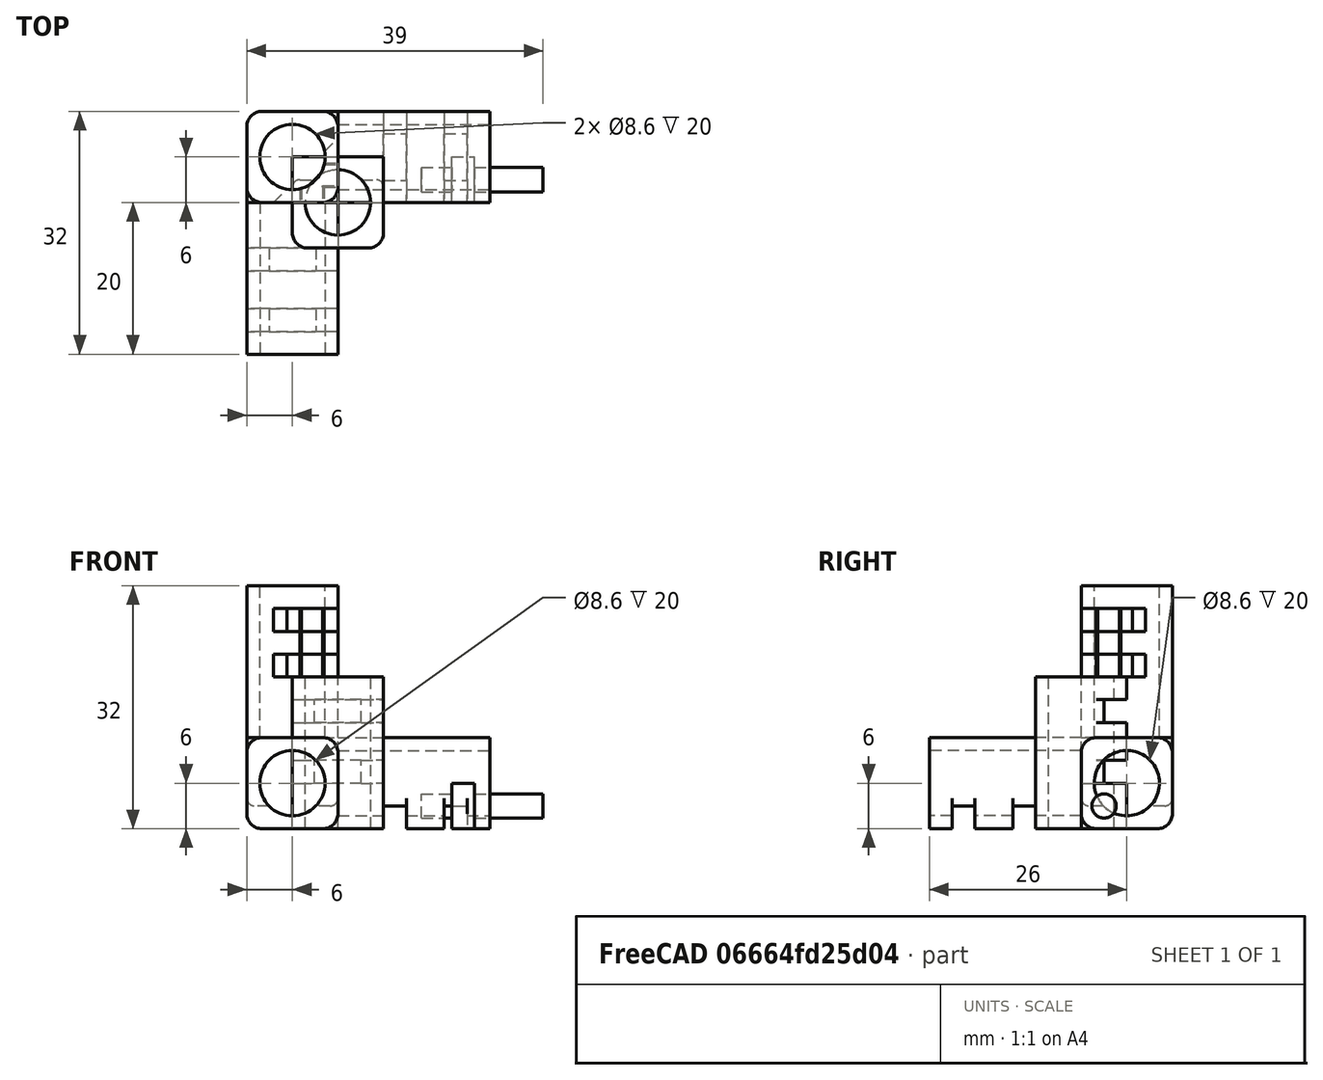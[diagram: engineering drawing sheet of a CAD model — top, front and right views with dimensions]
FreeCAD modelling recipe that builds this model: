
FCSTD DOCUMENT  (FreeCAD 0.18R14555 (Git shallow))
Label: tmp-ecnlose
License: All rights reserved
LicenseURL: http://en.wikipedia.org/wiki/All_rights_reserved
objects: Part::Box×12, Part::Fillet×7, Part::MultiFuse×5, Part::Cut×5, Part::Cylinder×4, Part::Feature×2
note: 35 computed .brp shape members not serialized (recipe doc carries the construction recipe); baked Part::Feature solids carry a one-line shape summary decoded from their .brp

FEATURE [Part::Cylinder] Cylinder
  Angle = 360
  AttacherType = Attacher::AttachEngine3D
  Height = 20
  Radius = 4.3
FEATURE [Part::Box] Box  label="Cube"
  AttacherType = Attacher::AttachEngine3D
  Height = 20
  Length = 12
  Placement = pos=(-6,-6,0) rot=(0,0,1;0rad)
  Width = 12
FEATURE [Part::Box] Box001  label="Cube001"
  AttacherType = Attacher::AttachEngine3D
  Height = 6
  Length = 3
  Placement = pos=(15,0,0) rot=(0,0,1;0rad)
  Width = 6
FEATURE [Part::Cylinder] Cylinder001
  Angle = 360
  AttacherType = Attacher::AttachEngine3D
  Height = 16
  Placement = pos=(11,3,3) rot=(0,1,0;1.5708rad)
  Radius = 1.6
FEATURE [Part::MultiFuse] Fusion
  Shapes = -> [Cylinder001,Box001]
FEATURE [Part::Cut] Cut
  Base = -> Box
  Tool = -> Cylinder
FEATURE [Part::Box] Box002  label="Cube002"
  AttacherType = Attacher::AttachEngine3D
  Height = 3
  Length = 12
  Placement = pos=(-6,3,14) rot=(0,0,1;0rad)
  Width = 3
FEATURE [Part::Box] Box003  label="Cube003"
  AttacherType = Attacher::AttachEngine3D
  Height = 3
  Length = 12
  Placement = pos=(-6,3,6) rot=(0,0,1;0rad)
  Width = 3
FEATURE [Part::MultiFuse] Fusion001
  Shapes = -> [Box003,Box002]
FEATURE [Part::Cut] Cut001
  Base = -> Cut
  Tool = -> Fusion001
FEATURE [Part::Fillet] Fillet
  Base = -> Cut001
  Edges = 2 edges r=2: [Edge12,Edge46]
FEATURE [Part::Fillet] Fillet001
  Base = -> Fillet
  Edges = 4 edges r=1: [Edge7,Edge10,Edge53,Edge54]
FEATURE [Part::Feature] Fillet001001  label="Fillet002"
  Placement = pos=(-6,1.3e-15,6) rot=(0,-0.707107,0.707107;3.14159rad)
  shape: bbox 12 x 20 x 12 mm, 23 faces (baked)
FEATURE [Part::Feature] Fillet001002  label="Fillet003"
  Placement = pos=(1.8e-15,6,6) rot=(0.57735,-0.57735,0.57735;4.18879rad)
  shape: bbox 20 x 12 x 12 mm, 23 faces (baked)
FEATURE [Part::Box] Box004  label="Cube004"
  AttacherType = Attacher::AttachEngine3D
  Height = 12
  Length = 12
  Placement = pos=(-12,0,0) rot=(0,0,1;0rad)
  Width = 12
FEATURE [Part::Cylinder] Cylinder002
  Angle = 360
  AttacherType = Attacher::AttachEngine3D
  Height = 20
  Placement = pos=(-6,6,12) rot=(0,0,1;0rad)
  Radius = 4.3
FEATURE [Part::Box] Box005  label="Cube005"
  AttacherType = Attacher::AttachEngine3D
  Height = 20
  Length = 12
  Placement = pos=(-12,0,12) rot=(0,0,1;0rad)
  Width = 12
FEATURE [Part::Cut] Cut002
  Base = -> Box005
  Tool = -> Cylinder002
FEATURE [Part::Box] Box006  label="Cube006"
  AttacherType = Attacher::AttachEngine3D
  Height = 3
  Length = 7
  Placement = pos=(-9.19239,-0.707107,26) rot=(0,0,1;5.49779rad)
  Width = 15
FEATURE [Part::Box] Box007  label="Cube007"
  AttacherType = Attacher::AttachEngine3D
  Height = 3
  Length = 7
  Placement = pos=(-9.19239,-0.707107,20) rot=(0,0,-1;0.785398rad)
  Width = 15
FEATURE [Part::MultiFuse] Fusion002
  Shapes = -> [Box006,Box007]
FEATURE [Part::Cut] Cut003
  Base = -> Cut002
  Tool = -> Fusion002
FEATURE [Part::Fillet] Fillet001003
  Base = -> Cut003
  Edges = 3 edges r=2: [Edge1,Edge3,Edge20]
FEATURE [Part::Fillet] Fillet001004
  Base = -> Fillet001003
  Edges = 3 edges r=2: [Edge21,Edge23,Edge28]
FEATURE [Part::Fillet] Fillet001005
  Base = -> Fillet001002
  Edges = 6 edges r=2: [Edge4,Edge9,Edge16,Edge27,Edge43,Edge66]
FEATURE [Part::Fillet] Fillet001006
  Base = -> Fillet001001
  Edges = 6 edges r=2: [Edge4,Edge9,Edge16,Edge27,Edge43,Edge66]
FEATURE [Part::Fillet] Fillet001007
  Base = -> Box004
  Edges = 3 edges r=2: [Edge3,Edge4,Edge11]
FEATURE [Part::Box] Box008  label="Cube008"
  AttacherType = Attacher::AttachEngine3D
  Height = 9
  Length = 2
  Placement = pos=(-2,2,20) rot=(0,0,1;0rad)
  Width = 0.2
FEATURE [Part::Box] Box009  label="Cube009"
  AttacherType = Attacher::AttachEngine3D
  Height = 9
  Length = 2
  Placement = pos=(-2,5,20) rot=(0,0,1;0rad)
  Width = 0.2
FEATURE [Part::Box] Box010  label="Cube010"
  AttacherType = Attacher::AttachEngine3D
  Height = 9
  Length = 2
  Placement = pos=(-2,2,20) rot=(0,0,1;4.71239rad)
  Width = 0.2
FEATURE [Part::Box] Box011  label="Cube011"
  AttacherType = Attacher::AttachEngine3D
  Height = 9
  Length = 2
  Placement = pos=(-5,2,20) rot=(0,0,-1;1.5708rad)
  Width = 0.2
FEATURE [Part::Cylinder] Cylinder003
  Angle = 360
  AttacherType = Attacher::AttachEngine3D
  Height = 20
  Placement = pos=(-6,6,12) rot=(0,0,1;0rad)
  Radius = 4.3
FEATURE [Part::MultiFuse] Fusion003
  Shapes = -> [Box008,Box010,Box009,Box011]
FEATURE [Part::Cut] Cut004
  Base = -> Fusion003
  Tool = -> Cylinder003
FEATURE [Part::MultiFuse] Fusion004
  Shapes = -> [Fillet001004,Fillet001005,Fillet001006,Fillet001007]
